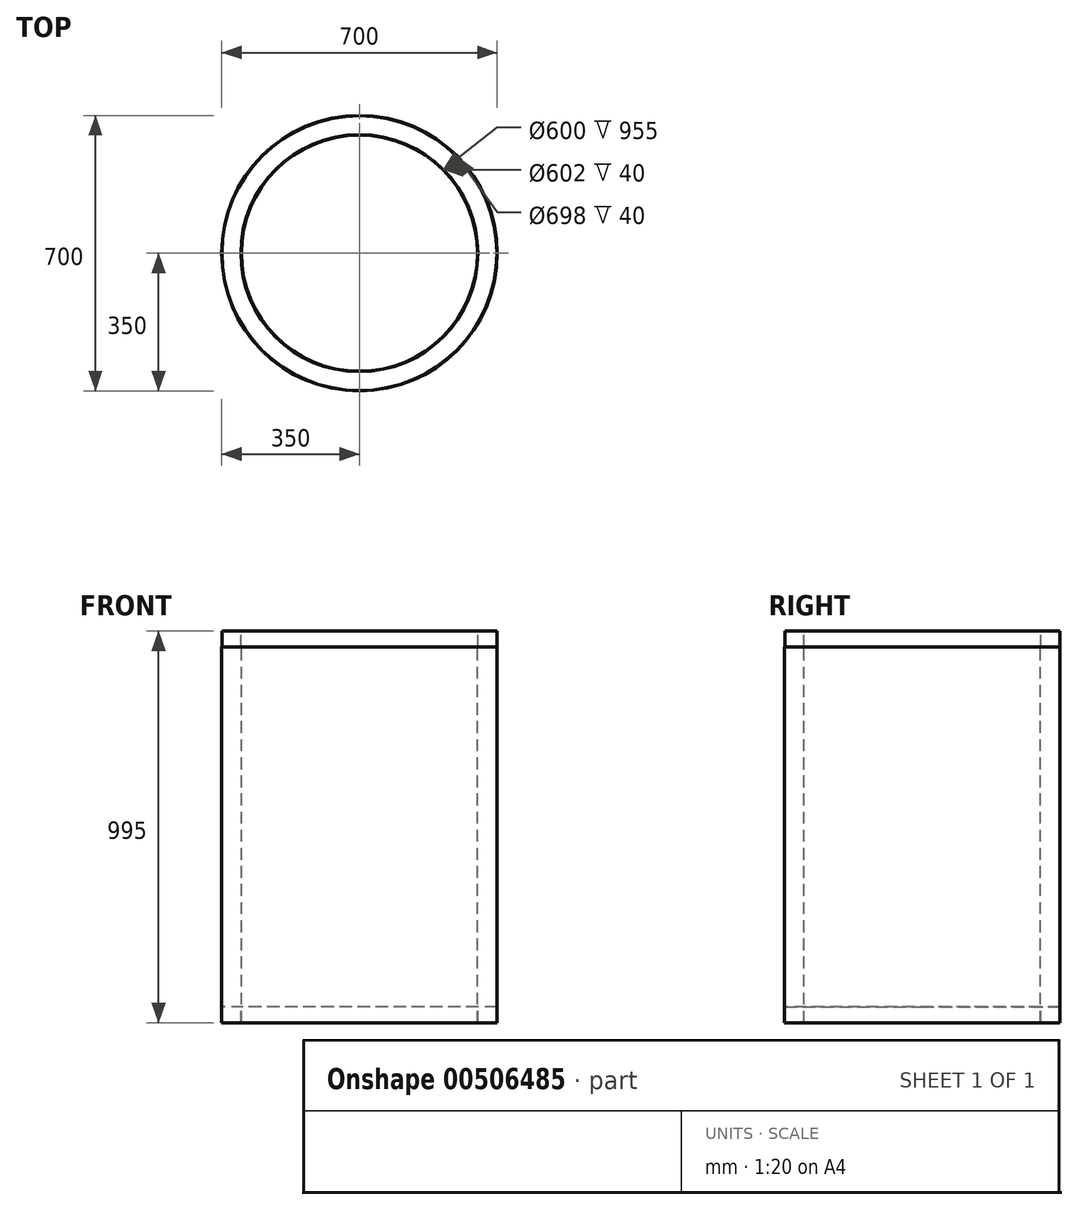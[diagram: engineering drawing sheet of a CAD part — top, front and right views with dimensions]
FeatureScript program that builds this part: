
annotation { "Feature Type Name" : "Feature", "Feature Type Description" : "" }
export const myFeature = defineFeature(function(context is Context, id is Id, definition is map)
    precondition{}
    {
        {
            var Q0;
            Q0=qCreatedBy(makeId("Front.planeOp"),FACE);
            var sketch = newSketch(context, id + "F0", { "sketchPlane" : qUnion([Q0])});
            skLineSegment(sketch, "E0", {"start": v(0, 452.89) * mm, "end": v(0, -450.9) * mm, "construction": true});
            skLineSegment(sketch, "E1", {"start": v(-300, -411.7) * mm, "end": v(-300, 543.3) * mm});
            skLineSegment(sketch, "E2", {"start": v(-300, 543.3) * mm, "end": v(-301, 543.3) * mm});
            skLineSegment(sketch, "E3", {"start": v(-301, 543.3) * mm, "end": v(-301, 583.3) * mm});
            skLineSegment(sketch, "E4", {"start": v(-301, 583.3) * mm, "end": v(-349, 583.3) * mm});
            skLineSegment(sketch, "E5", {"start": v(-349, 583.3) * mm, "end": v(-349, 543.3) * mm});
            skLineSegment(sketch, "E6", {"start": v(-349, 543.3) * mm, "end": v(-350, 543.3) * mm});
            skLineSegment(sketch, "E7", {"start": v(-350, 543.3) * mm, "end": v(-350, -411.7) * mm});
            skLineSegment(sketch, "E8", {"start": v(-350, -411.7) * mm, "end": v(-349, -411.7) * mm});
            skLineSegment(sketch, "E9", {"start": v(-349, -411.7) * mm, "end": v(-349, -371.7) * mm});
            skLineSegment(sketch, "E10", {"start": v(-349, -371.7) * mm, "end": v(-301, -371.7) * mm});
            skLineSegment(sketch, "E11", {"start": v(-301, -371.7) * mm, "end": v(-301, -411.7) * mm});
            skLineSegment(sketch, "E12", {"start": v(-301, -411.7) * mm, "end": v(-300, -411.7) * mm});
            skSolve(sketch);
        }
        {
            var Q0;
            Q0=qSketchRegion(id+"F0",true);
            var Q1;
            Q1=sQuery(id+"F0.wireOp",EDGE,"E0");
            revolve(context, id + "F1", {"entities" : qUnion([Q0]), "axis" : qUnion([Q1]), "revolveType" : RevolveType.FULL});
        }
    });
